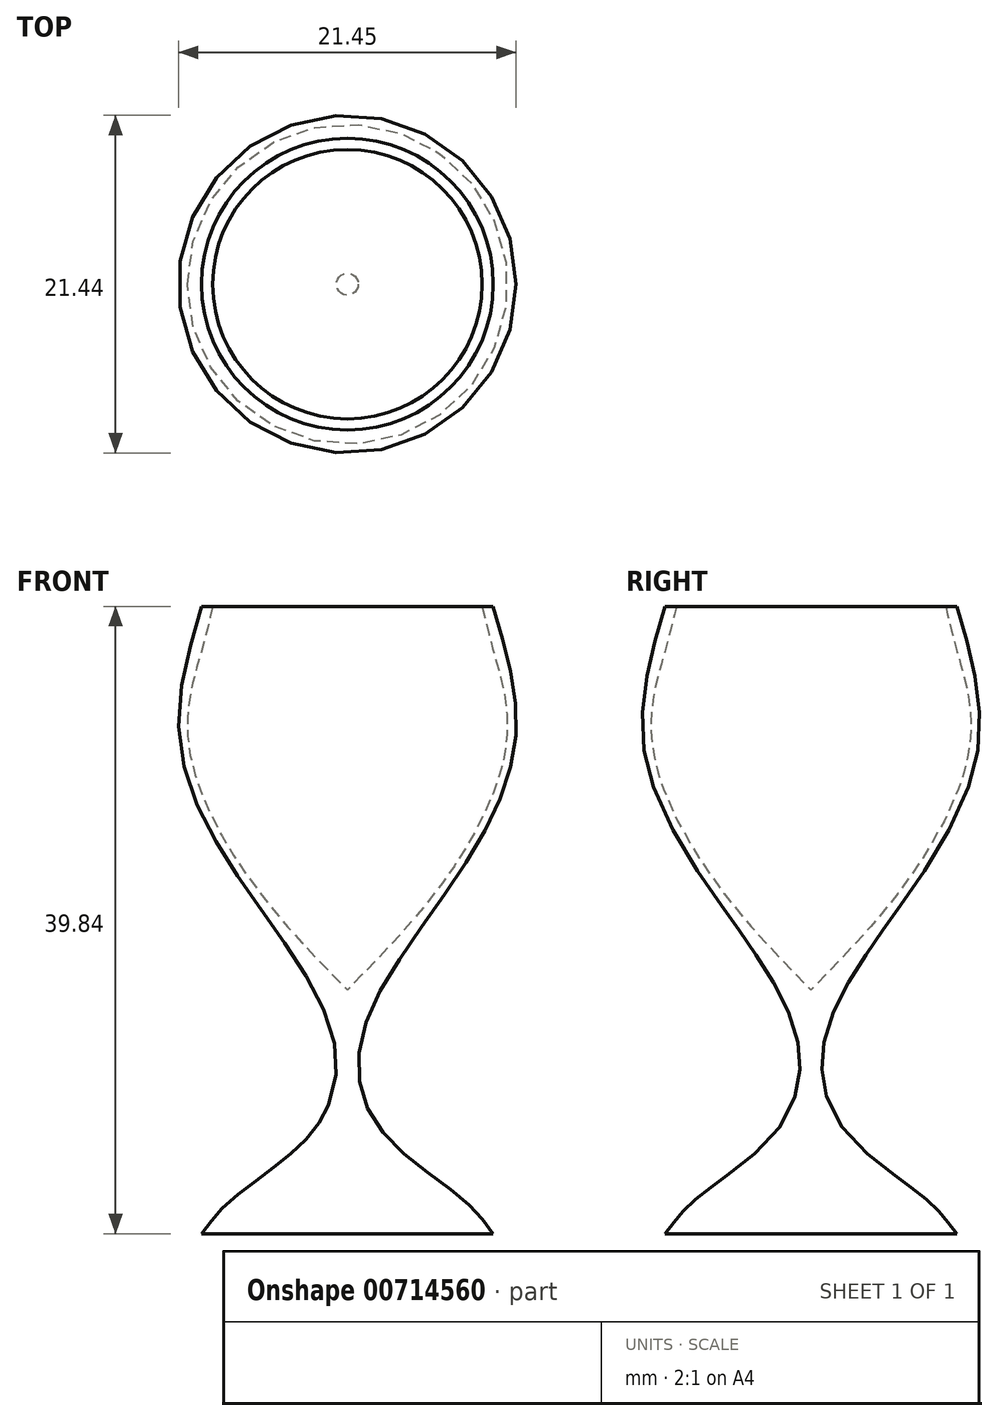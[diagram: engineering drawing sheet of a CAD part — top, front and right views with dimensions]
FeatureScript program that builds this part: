
annotation { "Feature Type Name" : "Feature", "Feature Type Description" : "" }
export const myFeature = defineFeature(function(context is Context, id is Id, definition is map)
    precondition{}
    {
        {
            var Q0;
            Q0=qCreatedBy(makeId("Front.planeOp"),FACE);
            var sketch = newSketch(context, id + "F0", { "sketchPlane" : qUnion([Q0])});
            skLineSegment(sketch, "E0", {"start": v(-26.98, 50.6) * mm, "end": v(-26.98, 10.77) * mm});
            skLineSegment(sketch, "E1", {"start": v(-26.98, 10.77) * mm, "end": v(-36.25, 10.77) * mm});
            skFitSpline(sketch, "E2", {"points": [v(-36.25, 10.77) * mm, v(-34.17, 13.08) * mm, v(-29.06, 17.41) * mm, v(-27.98, 23.6) * mm, v(-33.78, 33.21) * mm, v(-37.66, 42.12) * mm, v(-36.25, 50.6) * mm], "startDerivative": vector(15.32, 20.66) * mm, "endDerivative": vector(13.97, 47.29) * mm});
            skLineSegment(sketch, "E3", {"start": v(-36.25, 50.6) * mm, "end": v(-26.98, 50.6) * mm});
            skLineSegment(sketch, "E4", {"start": v(-26.98, 50.6) * mm, "end": v(-35.54, 50.6) * mm});
            skFitSpline(sketch, "E5", {"points": [v(-35.54, 50.6) * mm, v(-36.25, 47.8) * mm, v(-37.12, 42.21) * mm, v(-33.39, 33.57) * mm, v(-26.98, 26.26) * mm], "startDerivative": vector(-3.66, -15.64) * mm, "endDerivative": vector(22.13, -22.52) * mm});
            skSolve(sketch);
        }
        {
            var Q0;
            {var subQ0=sQuery(id+"F0.wireOp",EDGE,"E1");Q0=makeQuery(id+"F0.imprint","IMPRINT",FACE,{"disambiguationData":[TD([[makeQuery(id+"F0.imprint","IMPRINT",EDGE,{"derivedFrom":subQ0}),-1.0]])]});}
            var Q1;
            Q1=sQuery(id+"F0.wireOp",EDGE,"E0");
            revolve(context, id + "F1", {"surfaceOperationType" : NewSurfaceOperationType.NEW, "entities" : qUnion([Q0]), "axis" : qUnion([Q1]), "revolveType" : RevolveType.FULL});
        }
    });
